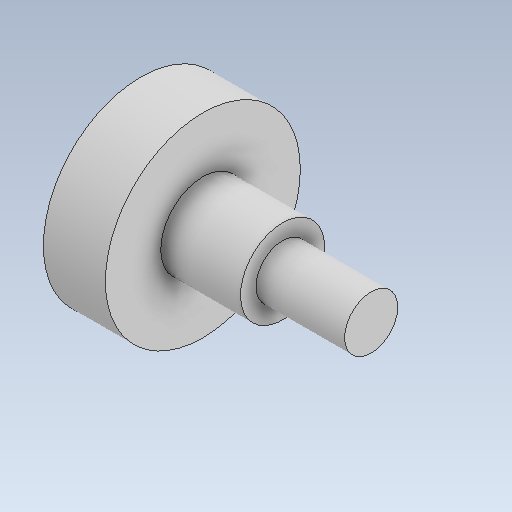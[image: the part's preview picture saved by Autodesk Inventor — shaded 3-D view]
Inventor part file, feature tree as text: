
AUTODESK INVENTOR PART (.ipt)
format: ipt  version: 2020 (Build 240168000, 168)  size: 115,200 bytes
history: native  units: mm
features: other x3, sketch x1
ambient origin geometry x8: Origin, YZ Plane, XZ Plane, XY Plane, X Axis, Y Axis, Z Axis, Center Point
bodies: Solid1 (feature_tree)
feature tree (4):
  other  "guia_MIR.ipt"
  other  "Solid1::guia_MIR.ipt"
  other  "TaggingFeature1"
  sketch  "Sketch1"  dims[d0=10.0mm]
